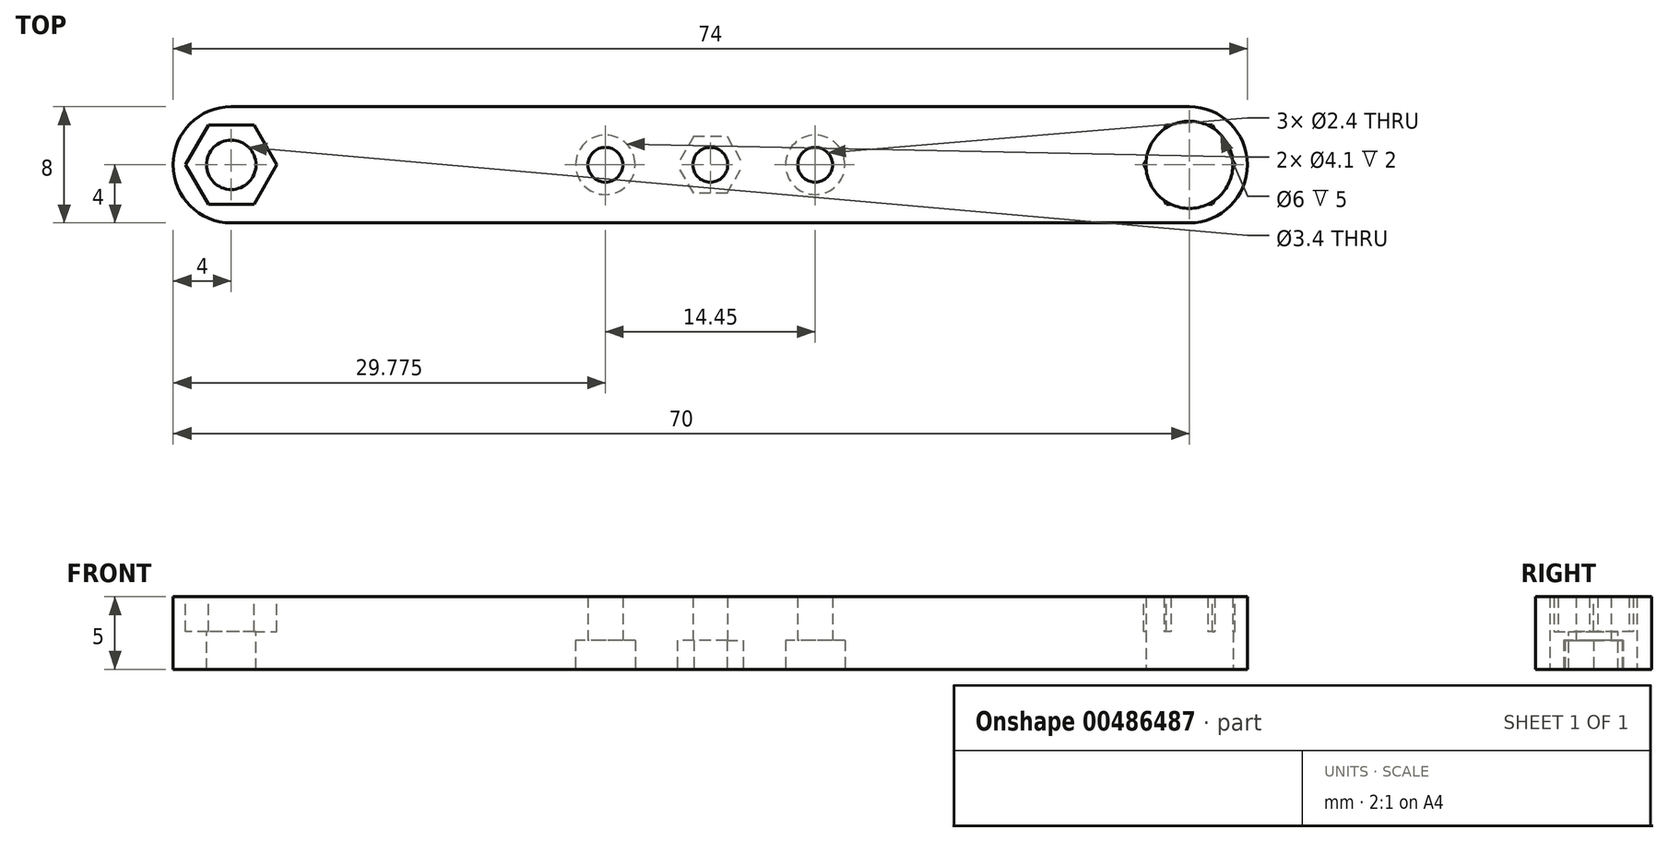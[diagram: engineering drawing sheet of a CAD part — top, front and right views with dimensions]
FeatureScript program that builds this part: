
annotation { "Feature Type Name" : "Feature", "Feature Type Description" : "" }
export const myFeature = defineFeature(function(context is Context, id is Id, definition is map)
    precondition{}
    {
        {
            var Q0;
            Q0=qCreatedBy(makeId("Top.planeOp"),FACE);
            var sketch = newSketch(context, id + "F0", { "sketchPlane" : qUnion([Q0])});
            skCircle(sketch, "E0", {"center": v(-33, 38) * mm, "radius": 1.7 * mm});
            skCircle(sketch, "E1.MirrorC", {"center": v(33, 38) * mm, "radius": 1.7 * mm});
            skCircle(sketch, "E2.MirrorC", {"center": v(-33, -38) * mm, "radius": 1.7 * mm});
            skCircle(sketch, "E3.MirrorC", {"center": v(33, -38) * mm, "radius": 1.7 * mm});
            skSolve(sketch);
        }
        {
            var Q0;
            Q0=qCreatedBy(makeId("Top.planeOp"),FACE);
            var sketch = newSketch(context, id + "F1", { "sketchPlane" : qUnion([Q0])});
            skCircle(sketch, "E4", {"center": v(-33, 38) * mm, "radius": 3 * mm});
            skCircle(sketch, "E5", {"center": v(-33, 38) * mm, "radius": 1.7 * mm});
            skCircle(sketch, "E6.MirrorC", {"center": v(33, 38) * mm, "radius": 1.7 * mm});
            skCircle(sketch, "E7.MirrorC", {"center": v(33, 38) * mm, "radius": 3 * mm});
            skLineSegment(sketch, "E8.bottom", {"start": v(-37, 42) * mm, "end": v(37, 42) * mm});
            skLineSegment(sketch, "E8.top", {"start": v(-37, 34) * mm, "end": v(37, 34) * mm});
            skLineSegment(sketch, "E8.left", {"start": v(-37, 42) * mm, "end": v(-37, 34) * mm});
            skLineSegment(sketch, "E8.right", {"start": v(37, 42) * mm, "end": v(37, 34) * mm});
            skSolve(sketch);
        }
        {
            var Q0;
            Q0=makeQuery(id+"F1.imprint","IMPRINT",FACE,{"disambiguationData":[TD([[makeQuery(id+"F1.imprint","IMPRINT",EDGE,{"derivedFrom":sQuery(id+"F1.wireOp",EDGE,"E4")}),-1.0]])]});
            var sketch = newSketch(context, id + "F2", { "sketchPlane" : qUnion([Q0])});
            skLineSegment(sketch, "E9", {"start": v(0, 38) * mm, "end": v(1.44, 35.5) * mm, "construction": true});
            skLineSegment(sketch, "E10", {"start": v(0, 38) * mm, "end": v(0, 36.02) * mm, "construction": true});
            skLineSegment(sketch, "E11", {"start": v(0, 36.02) * mm, "end": v(-1.14, 36.02) * mm});
            skLineSegment(sketch, "E12", {"start": v(-1.14, 36.02) * mm, "end": v(-2.28, 38) * mm});
            skLineSegment(sketch, "E13", {"start": v(-2.28, 38) * mm, "end": v(0, 38) * mm, "construction": true});
            skLineSegment(sketch, "E14.MirrorCS", {"start": v(-1.14, 39.97) * mm, "end": v(-2.28, 38) * mm});
            skLineSegment(sketch, "E15.MirrorCS", {"start": v(0, 39.97) * mm, "end": v(-1.14, 39.97) * mm});
            skLineSegment(sketch, "E16.MirrorCS", {"start": v(0, 36.02) * mm, "end": v(1.14, 36.02) * mm});
            skLineSegment(sketch, "E17.MirrorCS", {"start": v(1.14, 36.02) * mm, "end": v(2.28, 38) * mm});
            skLineSegment(sketch, "E18.MirrorCS", {"start": v(1.14, 39.97) * mm, "end": v(2.28, 38) * mm});
            skLineSegment(sketch, "E19.MirrorCS", {"start": v(0, 39.97) * mm, "end": v(1.14, 39.97) * mm});
            skSolve(sketch);
        }
        {
            var Q0;
            Q0=makeQuery(id+"F2.imprint","IMPRINT",FACE,{"disambiguationData":[TD([[makeQuery(id+"F2.imprint","IMPRINT",EDGE,{"derivedFrom":sQuery(id+"F2.wireOp",EDGE,"E11")}),1.0]])]});
            var sketch = newSketch(context, id + "F3", { "sketchPlane" : qUnion([Q0])});
            skCircle(sketch, "E20", {"center": v(-7.22, 38) * mm, "radius": 2.05 * mm});
            skCircle(sketch, "E21.MirrorC", {"center": v(7.22, 38) * mm, "radius": 2.05 * mm});
            skSolve(sketch);
        }
        {
            var Q0;
            Q0=makeQuery(id+"F1.imprint","IMPRINT",FACE,{"disambiguationData":[TD([[makeQuery(id+"F1.imprint","IMPRINT",EDGE,{"derivedFrom":sQuery(id+"F1.wireOp",EDGE,"E4")}),-1.0]])]});
            var sketch = newSketch(context, id + "F4", { "sketchPlane" : qUnion([Q0])});
            skCircle(sketch, "E22", {"center": v(-7.22, 38) * mm, "radius": 1.2 * mm});
            skCircle(sketch, "E23", {"center": v(0, 38) * mm, "radius": 1.2 * mm});
            skCircle(sketch, "E24.MirrorC", {"center": v(7.22, 38) * mm, "radius": 1.2 * mm});
            skSolve(sketch);
        }
        {
            var Q0;
            Q0=makeQuery(id+"F2.imprint","IMPRINT",FACE,{"disambiguationData":[TD([[makeQuery(id+"F2.imprint","IMPRINT",EDGE,{"derivedFrom":sQuery(id+"F2.wireOp",EDGE,"E11")}),1.0]])]});
            var Q1;
            Q1=makeQuery(id+"F2.imprint","IMPRINT",FACE,{"disambiguationData":[TD([[makeQuery(id+"F2.imprint","IMPRINT",EDGE,{"derivedFrom":sQuery(id+"F2.wireOp",EDGE,"E11")}),-1.0]])]});
            var Q2;
            Q2=makeQuery(id+"F2.imprint","IMPRINT",FACE,{"disambiguationData":[TD([[makeQuery(id+"F2.imprint","IMPRINT",EDGE,{"derivedFrom":makeQuery(id+"F1.imprint","IMPRINT",EDGE,{"derivedFrom":sQuery(id+"F1.wireOp",EDGE,"E4")})}),1.0]])]});
            var Q3;
            Q3=makeQuery(id+"F2.imprint","IMPRINT",FACE,{"disambiguationData":[TD([[makeQuery(id+"F2.imprint","IMPRINT",EDGE,{"derivedFrom":makeQuery(id+"F1.imprint","IMPRINT",EDGE,{"derivedFrom":sQuery(id+"F1.wireOp",EDGE,"E7.MirrorC")})}),-1.0]])]});
            extrude(context, id + "F5", {"entities" : qUnion([Q0, Q1, Q2, Q3]), "depth" : 5 * mm, "offsetDistance" : 25 * mm});
        }
        {
            var Q0;
            Q0=qSketchRegion(id+"F0",true);
            extrude(context, id + "F6", {"entities" : qUnion([Q0]), "operationType" : NewBodyOperationType.REMOVE, "oppositeDirection" : true, "depth" : 25 * mm, "offsetDistance" : 25 * mm, "symmetric" : true});
        }
        {
            var Q0;
            Q0=qSketchRegion(id+"F3",true);
            var Q1;
            Q1=sQuery(id+"F3.wireOp",EDGE,"E20");
            var Q2;
            Q2=sQuery(id+"F3.wireOp",EDGE,"E21.MirrorC");
            extrude(context, id + "F7", {"entities" : qUnion([Q0]), "operationType" : NewBodyOperationType.REMOVE, "surfaceEntities" : qUnion([Q1, Q2]), "depth" : 2 * mm, "offsetDistance" : 25 * mm});
        }
        {
            var Q0;
            Q0=qSketchRegion(id+"F2",true);
            extrude(context, id + "F8", {"entities" : qUnion([Q0]), "operationType" : NewBodyOperationType.REMOVE, "depth" : 2 * mm, "offsetDistance" : 25 * mm});
        }
        {
            var Q0;
            Q0=makeQuery(id+"F5.opExtrude","CAP_FACE",FACE,{"disambiguationData":[OSD([sQuery(id+"F1.wireOp",EDGE,"E8.bottom"),sQuery(id+"F1.wireOp",EDGE,"E8.top"),sQuery(id+"F1.wireOp",EDGE,"E8.left"),sQuery(id+"F1.wireOp",EDGE,"E8.right")])],"isStart":false});
            var sketch = newSketch(context, id + "F9", { "sketchPlane" : qUnion([Q0])});
            skLineSegment(sketch, "E25", {"start": v(-33, 38) * mm, "end": v(-33, 35.27) * mm, "construction": true});
            skLineSegment(sketch, "E26", {"start": v(-33, 35.27) * mm, "end": v(-33, 38) * mm, "construction": true});
            skLineSegment(sketch, "E27", {"start": v(-33, 38) * mm, "end": v(-32.14, 36.51) * mm, "construction": true});
            skLineSegment(sketch, "E28", {"start": v(-33, 35.27) * mm, "end": v(-34.57, 35.27) * mm});
            skLineSegment(sketch, "E29", {"start": v(-34.57, 35.27) * mm, "end": v(-36.15, 38) * mm});
            skLineSegment(sketch, "E30.MirrorCS", {"start": v(-31.43, 35.27) * mm, "end": v(-29.85, 38) * mm});
            skLineSegment(sketch, "E31.MirrorCS", {"start": v(-33, 35.27) * mm, "end": v(-31.43, 35.27) * mm});
            skLineSegment(sketch, "E32", {"start": v(-33, 38) * mm, "end": v(-36.15, 38) * mm, "construction": true});
            skLineSegment(sketch, "E33.MirrorCS", {"start": v(-34.57, 40.72) * mm, "end": v(-36.15, 38) * mm});
            skLineSegment(sketch, "E34.MirrorCS", {"start": v(-33, 40.72) * mm, "end": v(-34.57, 40.72) * mm});
            skLineSegment(sketch, "E35.MirrorCS", {"start": v(-33, 40.72) * mm, "end": v(-31.43, 40.72) * mm});
            skLineSegment(sketch, "E36.MirrorCS", {"start": v(-31.43, 40.72) * mm, "end": v(-29.85, 38) * mm});
            skLineSegment(sketch, "E37.MirrorCS", {"start": v(31.43, 35.27) * mm, "end": v(29.85, 38) * mm});
            skLineSegment(sketch, "E38.MirrorCS", {"start": v(31.43, 40.72) * mm, "end": v(29.85, 38) * mm});
            skLineSegment(sketch, "E39.MirrorCS", {"start": v(33, 40.72) * mm, "end": v(31.43, 40.72) * mm});
            skLineSegment(sketch, "E40.MirrorCS", {"start": v(33, 40.72) * mm, "end": v(34.57, 40.72) * mm});
            skLineSegment(sketch, "E41.MirrorCS", {"start": v(34.57, 40.72) * mm, "end": v(36.15, 38) * mm});
            skLineSegment(sketch, "E42.MirrorCS", {"start": v(34.57, 35.27) * mm, "end": v(36.15, 38) * mm});
            skLineSegment(sketch, "E43.MirrorCS", {"start": v(33, 35.27) * mm, "end": v(34.57, 35.27) * mm});
            skLineSegment(sketch, "E44.MirrorCS", {"start": v(33, 35.27) * mm, "end": v(31.43, 35.27) * mm});
            skSolve(sketch);
        }
        {
            var Q0;
            Q0=qSketchRegion(id+"F9",true);
            extrude(context, id + "F10", {"entities" : qUnion([Q0]), "operationType" : NewBodyOperationType.REMOVE, "oppositeDirection" : true, "depth" : 2.4 * mm, "offsetDistance" : 25 * mm});
        }
        {
            var Q0;
            Q0=makeQuery(id+"F5.opExtrude","SWEPT_EDGE",EDGE,{"disambiguationData":[OSD([sQuery(id+"F1.wireOp",EDGE,"E8.bottom"),sQuery(id+"F1.wireOp",EDGE,"E8.left")])]});
            var Q1;
            Q1=makeQuery(id+"F5.opExtrude","SWEPT_EDGE",EDGE,{"disambiguationData":[OSD([sQuery(id+"F1.wireOp",EDGE,"E8.top"),sQuery(id+"F1.wireOp",EDGE,"E8.left")])]});
            var Q2;
            Q2=makeQuery(id+"F5.opExtrude","SWEPT_EDGE",EDGE,{"disambiguationData":[OSD([sQuery(id+"F1.wireOp",EDGE,"E8.bottom"),sQuery(id+"F1.wireOp",EDGE,"E8.right")])]});
            var Q3;
            Q3=makeQuery(id+"F5.opExtrude","SWEPT_EDGE",EDGE,{"disambiguationData":[OSD([sQuery(id+"F1.wireOp",EDGE,"E8.top"),sQuery(id+"F1.wireOp",EDGE,"E8.right")])]});
            fillet(context, id + "F11", {"entities" : qUnion([Q0, Q1, Q2, Q3]), "radius" : 4 * mm, "tangentPropagation" : true, "allowEdgeOverflow" : false});
        }
        {
            var Q0;
            Q0=qSketchRegion(id+"F4",true);
            extrude(context, id + "F12", {"entities" : qUnion([Q0]), "operationType" : NewBodyOperationType.REMOVE, "endBound" : BoundingType.THROUGH_ALL, "depth" : 25 * mm, "offsetDistance" : 25 * mm});
        }
    });
